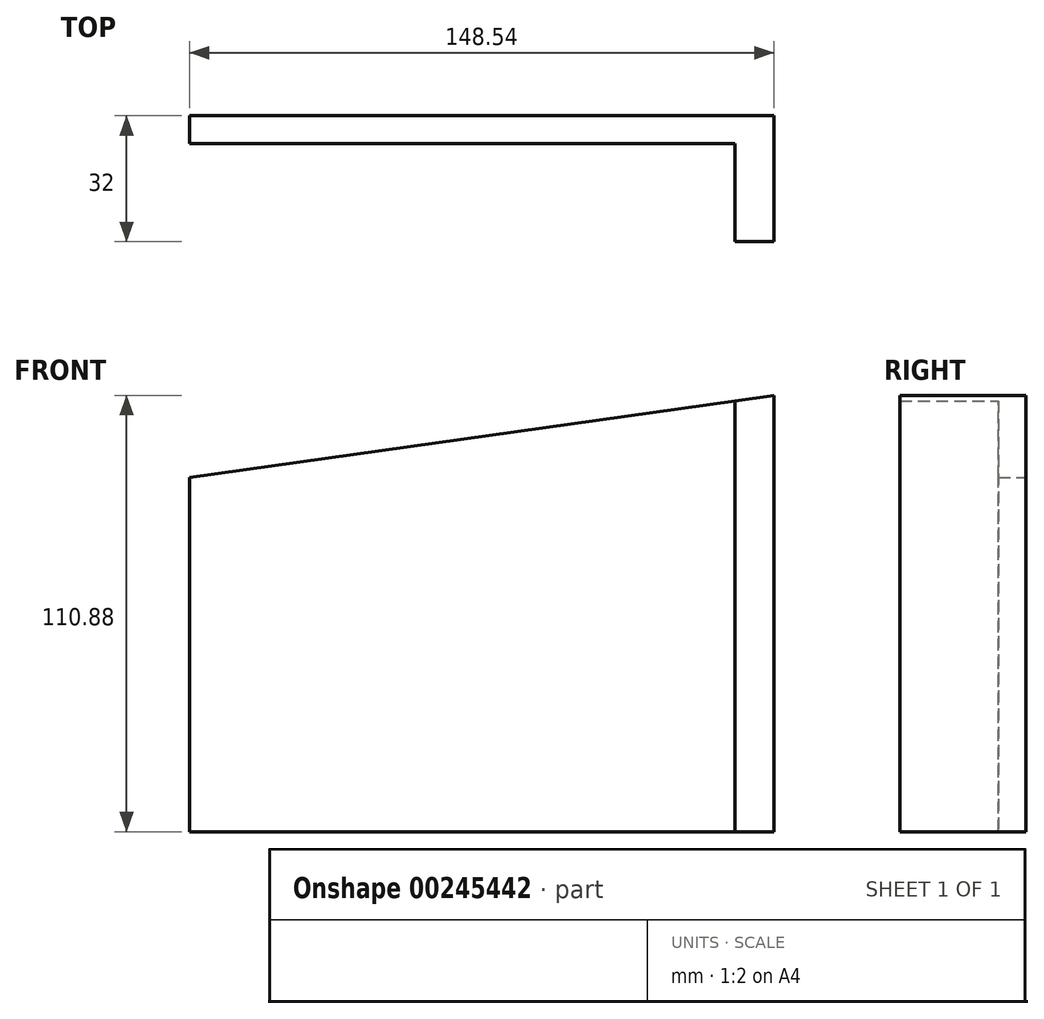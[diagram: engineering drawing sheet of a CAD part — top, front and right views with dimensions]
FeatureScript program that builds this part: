
annotation { "Feature Type Name" : "Feature", "Feature Type Description" : "" }
export const myFeature = defineFeature(function(context is Context, id is Id, definition is map)
    precondition{}
    {
        {
            var Q0;
            Q0=qCreatedBy(makeId("Front.planeOp"),FACE);
            var sketch = newSketch(context, id + "F0", { "sketchPlane" : qUnion([Q0])});
            skLineSegment(sketch, "E0", {"start": v(0, 0) * mm, "end": v(0, 90) * mm});
            skLineSegment(sketch, "E1", {"start": v(0, 90) * mm, "end": v(148.54, 110.88) * mm});
            skLineSegment(sketch, "E2", {"start": v(148.54, 110.88) * mm, "end": v(148.54, 0) * mm});
            skLineSegment(sketch, "E3", {"start": v(148.54, 0) * mm, "end": v(0, 0) * mm});
            skSolve(sketch);
        }
        {
            var Q0;
            Q0=qSketchRegion(id+"F0",true);
            extrude(context, id + "F1", {"entities" : qUnion([Q0]), "depth" : 7 * mm});
        }
        {
            var Q0;
            Q0=makeQuery(id+"F1.opExtrude","CAP_FACE",FACE,{"disambiguationData":[OSD([sQuery(id+"F0.wireOp",EDGE,"E0"),sQuery(id+"F0.wireOp",EDGE,"E1"),sQuery(id+"F0.wireOp",EDGE,"E2"),sQuery(id+"F0.wireOp",EDGE,"E3")])],"isStart":true});
            var sketch = newSketch(context, id + "F2", { "sketchPlane" : qUnion([Q0])});
            skLineSegment(sketch, "E4", {"start": v(-148.54, 110.88) * mm, "end": v(-148.54, 0) * mm});
            skLineSegment(sketch, "E5", {"start": v(-138.54, 109.47) * mm, "end": v(-148.54, 110.88) * mm});
            skLineSegment(sketch, "E6", {"start": v(-148.54, 0) * mm, "end": v(-138.54, 0) * mm});
            skLineSegment(sketch, "E7", {"start": v(-138.54, 0) * mm, "end": v(-138.54, 109.47) * mm});
            skSolve(sketch);
        }
        {
            var Q0;
            Q0=qSketchRegion(id+"F2",true);
            extrude(context, id + "F3", {"entities" : qUnion([Q0]), "operationType" : NewBodyOperationType.ADD, "oppositeDirection" : true, "depth" : (25 + 7) * mm});
        }
    });
